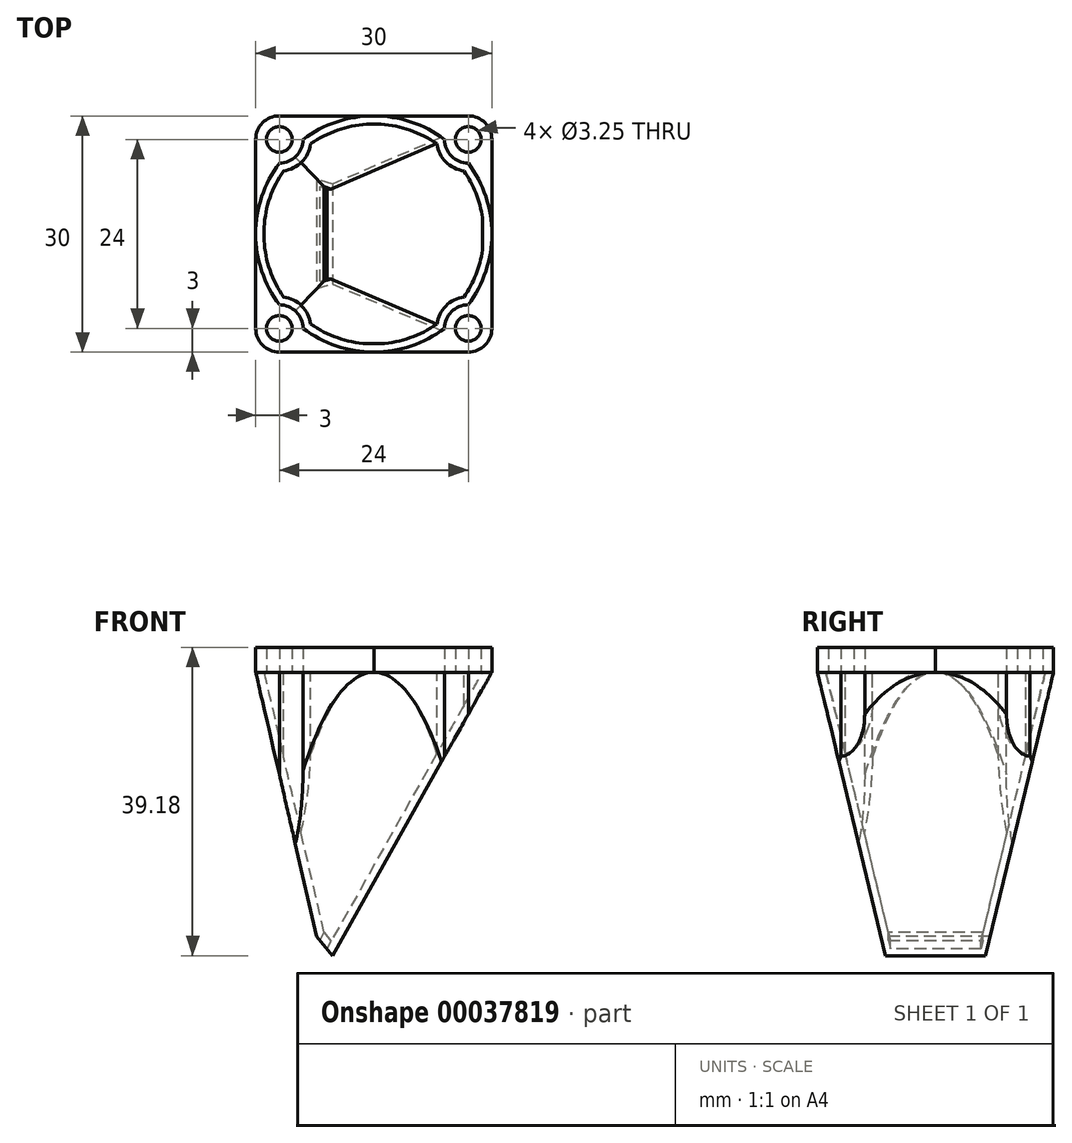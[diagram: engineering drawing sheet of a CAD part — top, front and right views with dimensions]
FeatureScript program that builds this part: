
annotation { "Feature Type Name" : "Feature", "Feature Type Description" : "" }
export const myFeature = defineFeature(function(context is Context, id is Id, definition is map)
    precondition{}
    {
        {
            var Q0;
            Q0=qCreatedBy(makeId("Top.planeOp"),FACE);
            var sketch = newSketch(context, id + "F0", { "sketchPlane" : qUnion([Q0])});
            skCircle(sketch, "E0", {"center": v(0, 15) * mm, "radius": 15 * mm});
            skLineSegment(sketch, "E1", {"start": v(0, 0) * mm, "end": v(0, 15) * mm, "construction": true});
            skSolve(sketch);
        }
        {
            var Q0;
            Q0 = qSketchRegion(id + "F0", true);
            extrude(context, id + "F1", {"entities" : qUnion([Q0]), "oppositeDirection" : true, "depth" : 50.8 * mm});
        }
        {
            var Q0;
            Q0=qCreatedBy(makeId("Front.planeOp"),FACE);
            var sketch = newSketch(context, id + "F2", { "sketchPlane" : qUnion([Q0])});
            skPoint(sketch, "E2", {"position": v(0, 0) * mm});
            skLineSegment(sketch, "E3.top", {"start": v(-15, -50.8) * mm, "end": v(15, -50.8) * mm});
            skLineSegment(sketch, "E3.left", {"start": v(-15, 0) * mm, "end": v(-15, -50.8) * mm});
            skLineSegment(sketch, "E3.right", {"start": v(15, 0) * mm, "end": v(15, -50.8) * mm});
            skLineSegment(sketch, "E4", {"start": v(15, 0) * mm, "end": v(-5.26, -36) * mm});
            skPoint(sketch, "E5.endSnap0", {"position": v(-6.26, -34.77) * mm});
            skLineSegment(sketch, "E6", {"start": v(-15, 0) * mm, "end": v(-7.26, -33.53) * mm});
            skLineSegment(sketch, "E7", {"start": v(15, 0) * mm, "end": v(-15, 0) * mm, "construction": true});
            skLineSegment(sketch, "E8", {"start": v(-5.26, -36) * mm, "end": v(-7.26, -33.53) * mm});
            skSolve(sketch);
        }
        {
            var Q0;
            Q0 = qSketchRegion(id + "F2", true);
            var Q1;
            Q1=makeQuery(id+"F1.opExtrude","SWEPT_FACE",FACE,{"disambiguationData":[OSD([sQuery(id+"F0.wireOp",EDGE,"E0")])]});
            extrude(context, id + "F3", {"entities" : qUnion([Q0]), "operationType" : NewBodyOperationType.REMOVE, "oppositeDirection" : true, "endBoundEntityFace" : qUnion([Q1]), "depth" : 50.8 * mm});
        }
        {
            var Q0;
            Q0=qCreatedBy(makeId("Right.planeOp"),FACE);
            var sketch = newSketch(context, id + "F4", { "sketchPlane" : qUnion([Q0])});
            skLineSegment(sketch, "E9.bottom", {"start": v(30, 0) * mm, "end": v(0, 0) * mm, "construction": true});
            skLineSegment(sketch, "E9.left", {"start": v(30, 0) * mm, "end": v(30, -36) * mm});
            skLineSegment(sketch, "E9.right", {"start": v(0, 0) * mm, "end": v(0, -36) * mm});
            skPoint(sketch, "E10", {"position": v(15, 0) * mm});
            skLineSegment(sketch, "E11", {"start": v(0, -36) * mm, "end": v(8.65, -36) * mm});
            skLineSegment(sketch, "E12", {"start": v(8.65, -36) * mm, "end": v(21.35, -36) * mm, "construction": true});
            skLineSegment(sketch, "E13", {"start": v(21.35, -36) * mm, "end": v(30, -36) * mm});
            skLineSegment(sketch, "E14", {"start": v(0, 0) * mm, "end": v(8.65, -36) * mm});
            skLineSegment(sketch, "E15", {"start": v(21.35, -36) * mm, "end": v(30, 0) * mm});
            skSolve(sketch);
        }
        {
            var Q0;
            Q0 = qSketchRegion(id + "F4", true);
            var Q1;
            Q1=makeQuery(id+"F1.opExtrude","SWEPT_FACE",FACE,{"disambiguationData":[OSD([sQuery(id+"F0.wireOp",EDGE,"E0")])]});
            extrude(context, id + "F5", {"entities" : qUnion([Q0]), "operationType" : NewBodyOperationType.REMOVE, "endBound" : BoundingType.UP_TO_SURFACE, "oppositeDirection" : true, "endBoundEntityFace" : qUnion([Q1]), "depth" : 25.4 * mm, "hasSecondDirection" : true, "secondDirectionOppositeDirection" : false, "secondDirectionDepth" : 25.4 * mm});
        }
        {
            var Q0;
            Q0=makeQuery(id+"F1.opExtrude","CAP_FACE",FACE,{"disambiguationData":[OSD([sQuery(id+"F0.wireOp",EDGE,"E0")])],"isStart":true});
            var sketch = newSketch(context, id + "F6", { "sketchPlane" : qUnion([Q0])});
            skLineSegment(sketch, "E16.rect.bottom", {"start": v(15, 0) * mm, "end": v(-15, 0) * mm, "construction": true});
            skLineSegment(sketch, "E16.rect.top", {"start": v(15, 30) * mm, "end": v(-15, 30) * mm, "construction": true});
            skLineSegment(sketch, "E16.rect.left", {"start": v(15, 0) * mm, "end": v(15, 30) * mm, "construction": true});
            skLineSegment(sketch, "E16.rect.right", {"start": v(-15, 0) * mm, "end": v(-15, 30) * mm, "construction": true});
            skPoint(sketch, "E16.rect.middle", {"position": v(0, 15) * mm});
            skCircle(sketch, "E17", {"center": v(12, 27) * mm, "radius": 3 * mm});
            skLineSegment(sketch, "E18.rect.bottom", {"start": v(12, 27) * mm, "end": v(-12, 27) * mm, "construction": true});
            skLineSegment(sketch, "E18.rect.top", {"start": v(12, 3) * mm, "end": v(-12, 3) * mm, "construction": true});
            skLineSegment(sketch, "E18.rect.left", {"start": v(12, 27) * mm, "end": v(12, 3) * mm, "construction": true});
            skLineSegment(sketch, "E18.rect.right", {"start": v(-12, 27) * mm, "end": v(-12, 3) * mm, "construction": true});
            skCircle(sketch, "E19", {"center": v(12, 3) * mm, "radius": 3 * mm});
            skCircle(sketch, "E20", {"center": v(-12, 3) * mm, "radius": 3 * mm});
            skCircle(sketch, "E21", {"center": v(-12, 27) * mm, "radius": 3 * mm});
            skSolve(sketch);
        }
        {
            var Q0;
            Q0 = qSketchRegion(id + "F6", true);
            var Q1;
            Q1=makeQuery(id+"F3.boolean.opBoolean","COPY",FACE,{"derivedFrom":makeQuery(id+"F3.opExtrude","SWEPT_FACE",FACE,{"disambiguationData":[OSD([sQuery(id+"F2.wireOp",EDGE,"E4")])]})});
            extrude(context, id + "F7", {"entities" : qUnion([Q0]), "operationType" : NewBodyOperationType.REMOVE, "endBound" : BoundingType.UP_TO_SURFACE, "oppositeDirection" : true, "endBoundEntityFace" : qUnion([Q1]), "depth" : 25.4 * mm});
        }
        {
            var Q0;
            Q0=makeQuery(id+"F1.opExtrude","CAP_FACE",FACE,{"disambiguationData":[OSD([sQuery(id+"F0.wireOp",EDGE,"E0")])],"isStart":true});
            shell(context, id + "F8", {"entities" : qUnion([Q0]), "thickness" : 1.03 * mm});
        }
        {
            var Q0;
            Q0=makeQuery(id+"F1.opExtrude","CAP_FACE",FACE,{"disambiguationData":[OSD([sQuery(id+"F0.wireOp",EDGE,"E0")])],"isStart":true});
            var sketch = newSketch(context, id + "F9", { "sketchPlane" : qUnion([Q0])});
            skLineSegment(sketch, "E22.rect.bottom", {"start": v(15, 0) * mm, "end": v(-15, 0) * mm});
            skLineSegment(sketch, "E22.rect.top", {"start": v(15, 30) * mm, "end": v(-15, 30) * mm});
            skLineSegment(sketch, "E22.rect.left", {"start": v(15, 0) * mm, "end": v(15, 30) * mm});
            skLineSegment(sketch, "E22.rect.right", {"start": v(-15, 0) * mm, "end": v(-15, 30) * mm});
            skPoint(sketch, "E22.rect.middle", {"position": v(0, 15) * mm});
            skCircle(sketch, "E23", {"center": v(12, 27) * mm, "radius": 1.63 * mm});
            skCircle(sketch, "E24", {"center": v(12, 3) * mm, "radius": 1.63 * mm});
            skCircle(sketch, "E25", {"center": v(-12, 3) * mm, "radius": 1.63 * mm});
            skCircle(sketch, "E26", {"center": v(-12, 27) * mm, "radius": 1.63 * mm});
            skSolve(sketch);
        }
        {
            var Q0;
            Q0=makeQuery(id+"F9.imprint","IMPRINT",FACE,{"disambiguationData":[TD([[makeQuery(id+"F9.imprint","IMPRINT",EDGE,{"derivedFrom":sQuery(id+"F9.wireOp",EDGE,"E24")}),-1.0]])]});
            var Q1;
            Q1=makeQuery(id+"F9.imprint","IMPRINT",FACE,{"disambiguationData":[TD([[makeQuery(id+"F9.imprint","IMPRINT",EDGE,{"derivedFrom":sQuery(id+"F9.wireOp",EDGE,"E25")}),-1.0]])]});
            var Q2;
            Q2=makeQuery(id+"F9.imprint","IMPRINT",FACE,{"disambiguationData":[TD([[makeQuery(id+"F9.imprint","IMPRINT",EDGE,{"derivedFrom":sQuery(id+"F9.wireOp",EDGE,"E23")}),-1.0]])]});
            var Q3;
            Q3=makeQuery(id+"F9.imprint","IMPRINT",FACE,{"disambiguationData":[TD([[makeQuery(id+"F9.imprint","IMPRINT",EDGE,{"derivedFrom":sQuery(id+"F9.wireOp",EDGE,"E26")}),-1.0]])]});
            var Q4;
            {var subQ18=sQuery(id+"F6.wireOp",EDGE,"E17");var subQ30=makeQuery(id+"F7.boolean.opBoolean","COPY",EDGE,{"derivedFrom":makeQuery(id+"F7.opExtrude","CAP_EDGE",EDGE,{"disambiguationData":[OSD([subQ18])],"isStart":true})});Q4=makeQuery(id+"F9.imprint","IMPRINT",FACE,{"disambiguationData":[TD([[makeQuery(id+"F9.imprint","IMPRINT",EDGE,{"derivedFrom":subQ30}),-1.0]])]});}
            extrude(context, id + "F10", {"entities" : qUnion([Q0, Q1, Q2, Q3, Q4]), "operationType" : NewBodyOperationType.ADD, "depth" : 3.17 * mm});
        }
        {
            var Q0;
            Q0=makeQuery(id+"F10.opExtrude","SWEPT_EDGE",EDGE,{"disambiguationData":[OSD([sQuery(id+"F9.wireOp",EDGE,"E22.rect.bottom"),sQuery(id+"F9.wireOp",EDGE,"E22.rect.left")])]});
            var Q1;
            Q1=makeQuery(id+"F10.opExtrude","SWEPT_EDGE",EDGE,{"disambiguationData":[OSD([sQuery(id+"F9.wireOp",EDGE,"E22.rect.bottom"),sQuery(id+"F9.wireOp",EDGE,"E22.rect.right")])]});
            var Q2;
            Q2=makeQuery(id+"F10.opExtrude","SWEPT_EDGE",EDGE,{"disambiguationData":[OSD([sQuery(id+"F9.wireOp",EDGE,"E22.rect.top"),sQuery(id+"F9.wireOp",EDGE,"E22.rect.right")])]});
            var Q3;
            Q3=makeQuery(id+"F10.opExtrude","SWEPT_EDGE",EDGE,{"disambiguationData":[OSD([sQuery(id+"F9.wireOp",EDGE,"E22.rect.top"),sQuery(id+"F9.wireOp",EDGE,"E22.rect.left")])]});
            fillet(context, id + "F11", {"entities" : qUnion([Q0, Q1, Q2, Q3]), "radius" : 3 * mm, "tangentPropagation" : true, "allowEdgeOverflow" : false});
        }
        {
            var Q0;
            Q0=makeQuery(id+"F3.boolean.opBoolean","COPY",FACE,{"derivedFrom":makeQuery(id+"F3.opExtrude","SWEPT_FACE",FACE,{"disambiguationData":[OSD([sQuery(id+"F2.wireOp",EDGE,"E4")])]})});
            var sketch = newSketch(context, id + "F12", { "sketchPlane" : qUnion([Q0])});
            skLineSegment(sketch, "E27.bottom", {"start": v(8.22, -11.3) * mm, "end": v(20.63, -11.3) * mm});
            skLineSegment(sketch, "E27.top", {"start": v(8.22, -13.02) * mm, "end": v(20.63, -13.02) * mm});
            skLineSegment(sketch, "E27.left", {"start": v(8.22, -11.3) * mm, "end": v(8.22, -13.02) * mm});
            skLineSegment(sketch, "E27.right", {"start": v(20.63, -11.3) * mm, "end": v(20.63, -13.02) * mm});
            skSolve(sketch);
        }
        {
            var Q0;
            Q0 = qSketchRegion(id + "F12", true);
            var Q1;
            Q1=makeQuery(id+"F8.opShell","OFFSET_FACE",FACE,{"disambiguationData":[OSD([sQuery(id+"F2.wireOp",EDGE,"E4")])]});
            extrude(context, id + "F13", {"entities" : qUnion([Q0]), "operationType" : NewBodyOperationType.REMOVE, "endBound" : BoundingType.UP_TO_SURFACE, "oppositeDirection" : true, "endBoundEntityFace" : qUnion([Q1]), "depth" : 25.4 * mm});
        }
        {
            var Q0;
            Q0=makeQuery(id+"F13.boolean.opBoolean","COPY",FACE,{"derivedFrom":makeQuery(id+"F13.opExtrude","SWEPT_FACE",FACE,{"disambiguationData":[OSD([sQuery(id+"F12.wireOp",EDGE,"E27.top")])]})});
            var sketch = newSketch(context, id + "F14", { "sketchPlane" : qUnion([Q0])});
            skLineSegment(sketch, "E28", {"start": v(12.04, 20.73) * mm, "end": v(10.72, 21) * mm});
            skLineSegment(sketch, "E29", {"start": v(12.04, 9.27) * mm, "end": v(10.72, 9) * mm});
            skLineSegment(sketch, "E30", {"start": v(10.72, 21) * mm, "end": v(10.72, 9) * mm});
            skLineSegment(sketch, "E31", {"start": v(12.04, 20.73) * mm, "end": v(12.04, 9.27) * mm});
            skSolve(sketch);
        }
        {
            var Q0;
            Q0 = qSketchRegion(id + "F14", true);
            var Q1;
            Q1=makeQuery(id+"F3.boolean.opBoolean","COPY",FACE,{"derivedFrom":makeQuery(id+"F3.opExtrude","SWEPT_FACE",FACE,{"disambiguationData":[OSD([sQuery(id+"F2.wireOp",EDGE,"E8")])]})});
            extrude(context, id + "F15", {"entities" : qUnion([Q0]), "operationType" : NewBodyOperationType.REMOVE, "endBound" : BoundingType.UP_TO_SURFACE, "oppositeDirection" : true, "endBoundEntityFace" : qUnion([Q1]), "depth" : 25.4 * mm});
        }
        {
            var Q0;
            Q0=makeQuery(id+"F13.boolean.opBoolean","COPY",FACE,{"derivedFrom":makeQuery(id+"F13.opExtrude","SWEPT_FACE",FACE,{"disambiguationData":[OSD([sQuery(id+"F12.wireOp",EDGE,"E27.top")])]})});
            var Q1;
            Q1=makeQuery(id+"F13.boolean.opBoolean","COPY",FACE,{"derivedFrom":makeQuery(id+"F13.opExtrude","SWEPT_FACE",FACE,{"disambiguationData":[OSD([sQuery(id+"F12.wireOp",EDGE,"E27.bottom")])]})});
            extrude(context, id + "F16", {"entities" : qUnion([Q0]), "operationType" : NewBodyOperationType.ADD, "endBound" : BoundingType.UP_TO_SURFACE, "endBoundEntityFace" : qUnion([Q1]), "depth" : 25.4 * mm});
        }
    });
